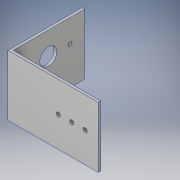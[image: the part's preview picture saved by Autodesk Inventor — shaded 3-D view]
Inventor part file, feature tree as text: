
AUTODESK INVENTOR PART (.ipt)
format: ipt  version: 2019 (Build 230136000, 136)  size: 143,872 bytes
history: native  units: mm
features: sketch x5, extrude x3, hole x2, other x1
ambient origin geometry x8: Origin, YZ Plane, XZ Plane, XY Plane, X Axis, Y Axis, Z Axis, Center Point
bodies: Body1 (feature_tree)
feature tree (11):
  other  "ソリッド1"
  extrude  "押し出し1"  Depth=65.0mm
  extrude  "押し出し2"  Depth=45.0mm
  extrude  "押し出し3"  Depth=2.0mm TaperAngle=0.0deg
  hole  "穴1"  [1 undecoded]
  hole  "穴2"  [1 undecoded]
  sketch  "スケッチ1"
  sketch  "スケッチ2"
  sketch  "スケッチ3"
  sketch  "スケッチ4"
  sketch  "スケッチ5"
note: 2 required parameter values undecoded (feature->parameter linkage not recoverable at this tier; creation-order binding heuristic only, values carry confidence <= 0.55)
